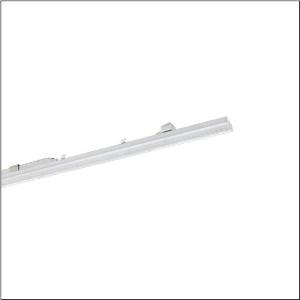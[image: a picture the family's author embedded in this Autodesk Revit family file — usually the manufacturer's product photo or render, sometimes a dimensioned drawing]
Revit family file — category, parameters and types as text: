
# Revit family: tl_l_5wd7a8h0b2b5
name_source: partatom
category: Lighting Fixtures
units: mm (PartAtom-declared; Revit-internal decimal feet)

## family parameters
Cut with Voids When Loaded = No
Host = Face
Light Source = No
Part Type = Normal
Room Calculation Point = No
Round Connector Dimension = Use Diameter
Shared = No

## types (1)
- --- (1 x LED, 850 lm, 4.5 W, 4000K)
    Apparent Load = 5 VA
    CIE Flux Codes = 49 84 98 100 100
    Color Rendering = 80
    Color Temperature = 4000K
    Default Elevation = 1800 mm
    Description = TL L, luminaire insert, of sheet steel, galvanised, coil coated, white, length: 1.500mm, width: 66mm, height: 67mm, micro fuse,LED rated luminous flux: 4.990lm, light colour: 840, control gear: emergency light, with terminal, 3-pole, mains connection: 230..240V, AC, 50/60Hz, rated input power: 34W, primary optical cover: cover, of PMMA, light emission: direct distribution, protection rating (complete): as luminaire, insulation class (complete): insulation class I (protective earthing), certification: CE, impact resistance: IK06, permissible ambient temperature for indoor applications: +5..+35°C, packaging unit: 1 piece
    Height = 120 mm
    Lamp = 1 x LED
    Lamp Light Flux = 850 lm
    Lamp Power = 4.5 W
    Lamp count = 1
    Length = 1690 mm
    Luminous efficacy = 189 lm/W
    Manufacturer = Siteco
    ModVariant = No
    Model = 5WD7A8H0B2B5
    Mounting Place = Ceiling
    Mounting Type = Pendant
    Number of Poles = 1
    OnlyDefault = Yes
    Power Factor = 1
    Product Name = TL L
    Product group = luminaire insert
    ProductGroupID = 901
    Protection Class = Protection class I
    Protection Degree = Degree of protection
    RLX_Detail_Level = 1
    RLX_Emergency_Light_Flux = 0 lm
    RLX_Emergency_Type = 0
    RLX_Emergency_Type_DB = No
    RlxData = <blob elided: 17345 chars, md5=8e036c52>
    Socket = socket
    Standby Power = 0 W
    System Light Flux = 850 lm
    System Power = 5 W
    Type Comments = : emergency light operation: 3 h
    Type Image = l_1294382.jpg
    URL = http://relux.com
    VarID = @adj_012049
    Voltage = 0 V
    Weight = 0.00 kg
    Width = 208 mm

## geometry (parser evidence)
native form markers: Blend x4, Sweep x12
no freeform markers — native parametric forms only
